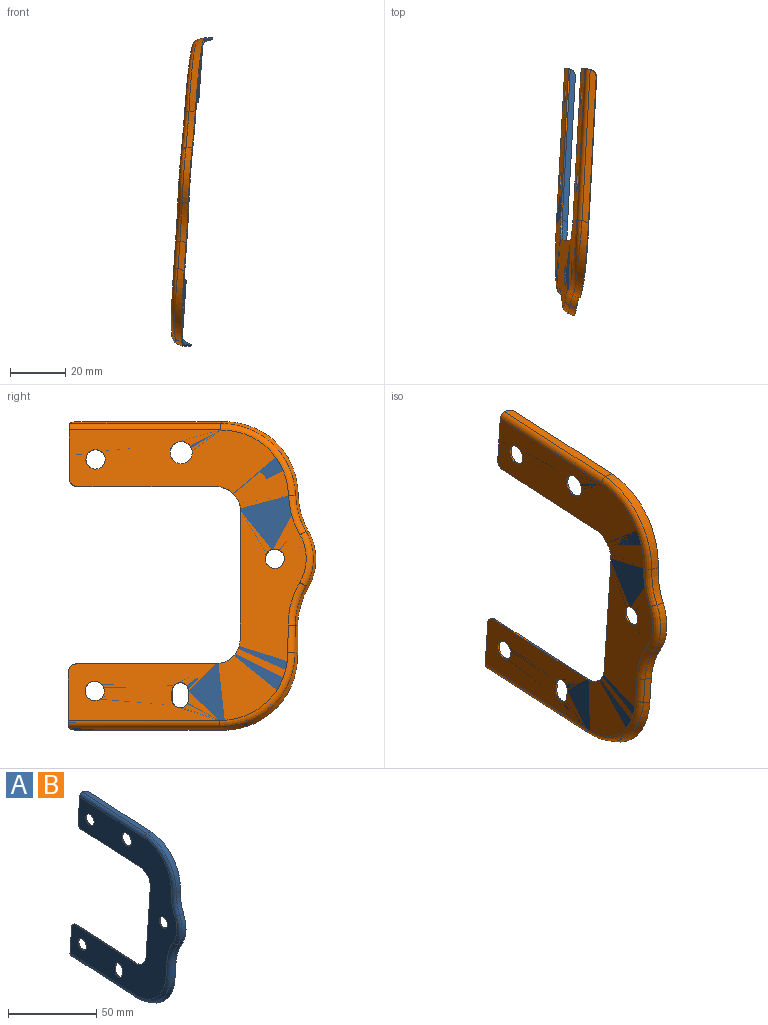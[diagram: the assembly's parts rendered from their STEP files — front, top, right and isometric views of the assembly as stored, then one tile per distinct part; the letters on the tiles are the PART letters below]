
ASSEMBLY  parts=2 mates=1
PART A: 54 faces, bbox 18.4x97.2x115.3 mm
  f0: cylinder r=2mm len=9.88mm, axis (-0.07,0,-1), area 24mm2, adj f8,f42,f46,f47
  f1: cylinder r=2.6mm len=9.91mm, axis (-0.07,0,-1), area 31.2mm2, adj f2,f24,f30,f33
  f2: bspline ~15.66x6.52mm, area 48.7mm2, adj f1,f3,f24,f32
  f3: bspline ~20.07x5.07mm, area 62.3mm2, adj f2,f24,f35,f36
  f4: plane 55.51x5mm, normal (-0.41,0.02,-0.91), area 132.3mm2, adj f25,f31,f37
  f5: cylinder r=30.6mm len=14.88mm, axis (-0.91,0.39,0.16), area 37.2mm2, adj f12,f13,f14,f42,f43,f46
  f6: cylinder r=2mm len=54.77mm, axis (-0.05,-1,0), area 133.7mm2, adj f18,f26,f29,f47
  f7: cylinder r=2.6mm len=54.79mm, axis (-0.05,-1,0), area 173.8mm2, adj f11,f15,f18,f24
  f8: bspline ~27.23x27.12mm, area 92.9mm2, adj f0,f17,f45,f47
  f9: bspline ~28.9x27.6mm, area 112.7mm2, adj f21,f26,f27,f29
  f10: bspline ~29.47x28.15mm, area 115mm2, adj f11,f15,f21,f34
  f11: bspline ~27.58x26.49mm, area 119.2mm2, adj f7,f10,f24,f36
  f12: bspline ~10.41x1.01mm, area 6.3mm2, adj f5,f13,f30,f39,f46
  f13: bspline ~14.35x4.47mm, area 8.9mm2, adj f5,f12,f14,f32
  f14: bspline ~20.44x3.35mm, area 12.7mm2, adj f5,f13,f20,f27,f35,f43
  f15: plane 55.54x5.12mm, normal (-0.28,0.01,0.96), area 134.4mm2, adj f7,f10,f19
  f16: bspline ~19.49x4.48mm, area 47mm2, adj f28,f42,f43,f47
  f17: cylinder r=2mm len=54.71mm, axis (0.05,1,0), area 133.6mm2, adj f8,f38,f44,f47
  f18: bspline ~2.43x2.12mm, area 1.7mm2, adj f6,f7,f19,f26,f41,f47
  f19: bspline ~55.55x3.02mm, area 33.8mm2, adj f15,f18,f21,f26
  f20: bspline ~13.57x4.36mm, area 8.4mm2, adj f14,f21,f27,f34
  f21: bspline ~27.16x26.49mm, area 25.1mm2, adj f9,f10,f19,f20,f26,f27
  f22: cylinder r=3.5mm len=7.02mm, axis (1,-0.05,-0.07), area 13.2mm2, adj f24,f47
  f23: cylinder r=3.5mm len=7.02mm, axis (1,-0.05,-0.07), area 13.2mm2, adj f24,f47
  f24: plane 105.37x86.4mm, normal (-1,0.05,0.07), area 4078.7mm2, adj f1,f2,f3,f7,f11,f22,f23,f25
  f25: cylinder r=2.6mm len=54.73mm, axis (0.05,1,0), area 173.7mm2, adj f4,f24,f33,f38
  f26: offset ~67.86x7.57mm, area 132.3mm2, adj f6,f9,f18,f19,f21
  f27: cylinder r=30.6mm len=13.7mm, axis (0.92,-0.39,0.03), area 34.8mm2, adj f9,f14,f20,f21,f28,f43
  f28: bspline ~14.49x5.88mm, area 35mm2, adj f16,f27,f29,f47
  f29: bspline ~26.99x25.94mm, area 90.6mm2, adj f6,f9,f28,f47
  f30: plane 10.78x2.9mm, normal (-0.39,-0.92,0.02), area 24.6mm2, adj f1,f12,f31,f32
  f31: cylinder r=29mm len=29.66mm, axis (0.85,-0.37,-0.38), area 118mm2, adj f4,f30,f33,f39
  f32: cylinder r=30mm len=14.54mm, axis (-0.91,0.39,0.16), area 36.1mm2, adj f2,f13,f30,f35
  f33: bspline ~27.8x27.31mm, area 122.2mm2, adj f1,f24,f25,f31
  f34: cylinder r=30mm len=13.42mm, axis (0.92,-0.39,0.03), area 34mm2, adj f10,f20,f35,f36
  f35: cone r=342.02mm half-angle=20deg, axis (1,-0.05,-0.07), area 51.3mm2, adj f3,f14,f32,f34
  f36: bspline ~14.35x6.39mm, area 45mm2, adj f3,f11,f24,f34
  f37: bspline ~55.53x3.11mm, area 33.9mm2, adj f4,f38,f39,f44
  f38: bspline ~2.56x1.79mm, area 1.7mm2, adj f17,f25,f37,f40,f44,f47
  f39: bspline ~27.37x27.24mm, area 25.6mm2, adj f12,f31,f37,f44,f45,f46
  f40: extruded ~17.98x1.85mm, area 10.8mm2, adj f24,f38,f41,f47
  f41: bspline ~87.21x62.33mm, area 120.1mm2, adj f18,f24,f40,f47
  f42: bspline ~15.61x5.98mm, area 37.9mm2, adj f0,f5,f16,f47
  f43: offset ~25.45x7.03mm, area 49.9mm2, adj f5,f14,f16,f27
  f44: offset ~67.82x7.43mm, area 132.3mm2, adj f17,f37,f38,f39,f45
  f45: cylinder r=28.4mm len=29.09mm, axis (0.85,-0.37,-0.38), area 115.5mm2, adj f8,f39,f44,f46
  f46: offset ~14.13x4.77mm, area 24.6mm2, adj f0,f5,f12,f39,f45
  f47: plane 105.37x86.4mm, normal (1,-0.05,-0.07), area 4158mm2, adj f0,f6,f8,f16,f17,f18,f22,f23
  f48: cylinder r=3.5mm len=7.02mm, axis (1,-0.05,-0.07), area 13.2mm2, adj f24,f47
  f49: cylinder r=4mm len=8.02mm, axis (-1,0.05,0.07), area 15.1mm2, adj f24,f47
  f50: plane 3.03x0.81mm, normal (-0.05,-1,0), area 1.8mm2, adj f24,f47,f51,f52
  f51: cylinder r=3mm len=6.02mm, axis (-1,0.05,0.07), area 5.7mm2, adj f24,f47,f50,f53
  f52: cylinder r=3mm len=6.02mm, axis (-1,0.05,0.07), area 5.7mm2, adj f24,f47,f50,f53
  f53: plane 3.03x0.81mm, normal (0.05,1,0), area 1.8mm2, adj f24,f47,f51,f52
PART B: same geometry as A
PLACE A t=(-1131.26,1319.64,-829.07)mm
PLACE B t=(-1131.26,1319.64,-829.07)mm
MATE fastened B.f48 <-> A.f48  axis (-1,0.05,0.07) through (2387,632.37,-1068.1)mm
